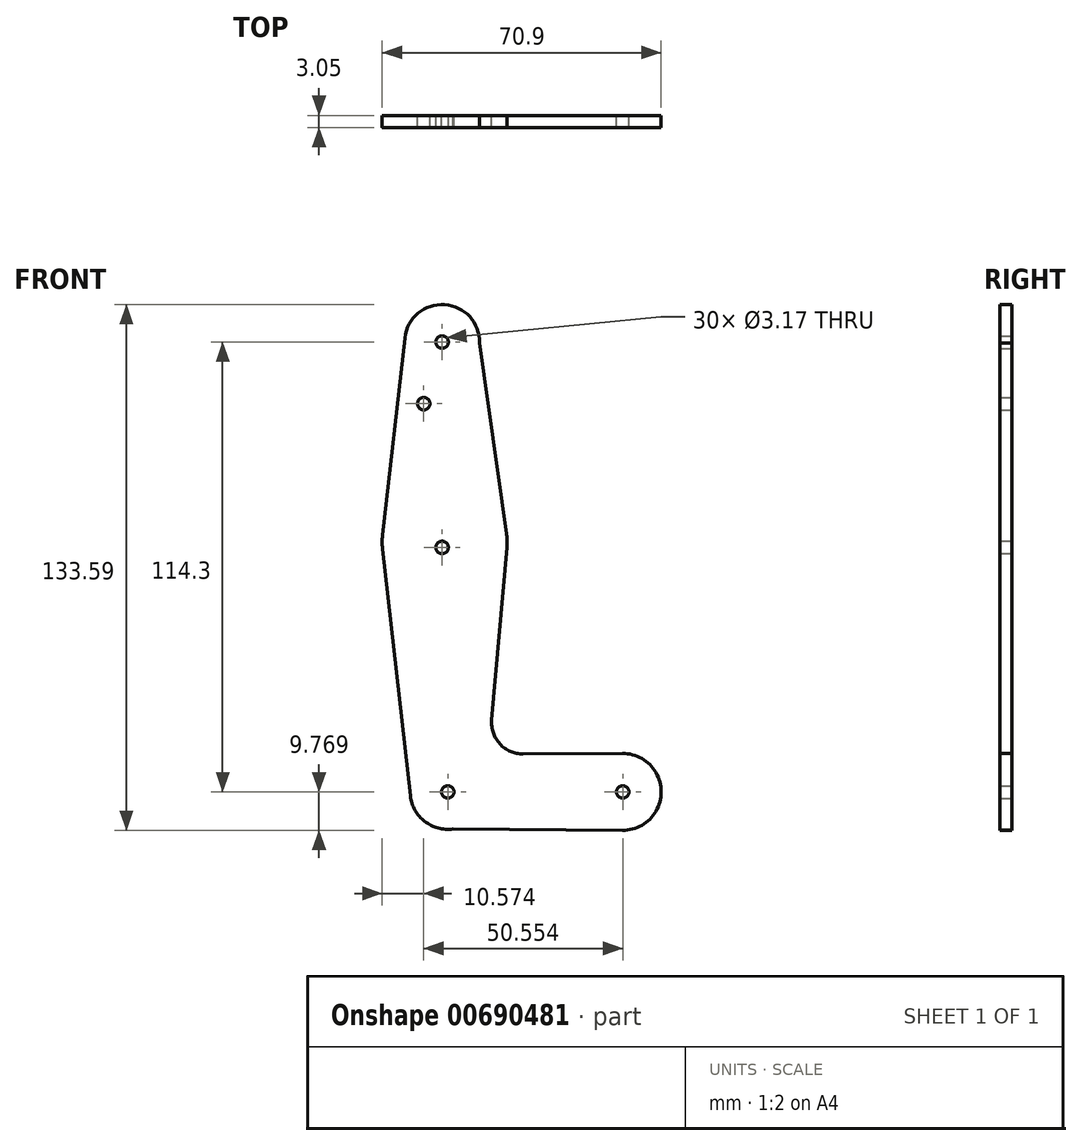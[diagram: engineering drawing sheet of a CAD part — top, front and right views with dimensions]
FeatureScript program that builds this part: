
annotation { "Feature Type Name" : "Feature", "Feature Type Description" : "" }
export const myFeature = defineFeature(function(context is Context, id is Id, definition is map)
    precondition{}
    {
        {
            var Q0;
            Q0=qCreatedBy(makeId("Front.planeOp"),FACE);
            var sketch = newSketch(context, id + "F0", { "sketchPlane" : qUnion([Q0])});
            skLineSegment(sketch, "E0", {"start": v(0, 52.19) * mm, "end": v(1.44, -62.11) * mm, "construction": true});
            skLineSegment(sketch, "E1", {"start": v(1.44, -62.11) * mm, "end": v(45.89, -62.11) * mm, "construction": true});
            skCircle(sketch, "E2", {"center": v(0, 52.19) * mm, "radius": 9.53 * mm});
            skCircle(sketch, "E3", {"center": v(1.44, -62.11) * mm, "radius": 9.53 * mm});
            skCircle(sketch, "E4", {"center": v(45.89, -62.11) * mm, "radius": 9.77 * mm});
            skCircle(sketch, "E5", {"center": v(0.64, 1.39) * mm, "radius": 15.88 * mm});
            skLineSegment(sketch, "E6", {"start": v(-9.46, 53.26) * mm, "end": v(-15.14, 3.17) * mm});
            skLineSegment(sketch, "E7", {"start": v(9.52, 51.98) * mm, "end": v(16.36, 3.6) * mm});
            skLineSegment(sketch, "E8", {"start": v(-15.14, -0.4) * mm, "end": v(-8.03, -63.18) * mm});
            skLineSegment(sketch, "E9", {"start": v(16.45, 0) * mm, "end": v(12.6, -43.84) * mm});
            skLineSegment(sketch, "E10", {"start": v(20.57, -52.48) * mm, "end": v(45.83, -52.34) * mm});
            skLineSegment(sketch, "E11", {"start": v(0, -71.53) * mm, "end": v(47.79, -71.9) * mm});
            skCircle(sketch, "E12", {"center": v(0, 52.19) * mm, "radius": 1.59 * mm});
            skCircle(sketch, "E13", {"center": v(0, 0) * mm, "radius": 1.59 * mm});
            skCircle(sketch, "E14", {"center": v(1.44, -62.11) * mm, "radius": 1.59 * mm});
            skCircle(sketch, "E15", {"center": v(45.89, -62.11) * mm, "radius": 1.59 * mm});
            skCircle(sketch, "E16", {"center": v(-4.67, 36.53) * mm, "radius": 1.59 * mm});
            skArc(sketch, "E17.filletArc", {"start": v(12.6, -43.84) * mm, "mid": v(14.68, -49.92) * mm, "end": v(20.57, -52.48) * mm});
            skSolve(sketch);
        }
        {
            var Q0;
            Q0 = qSketchRegion(id + "F0", true);
            extrude(context, id + "F1", {"entities" : qUnion([Q0]), "depth" : 3.05 * mm, "offsetDistance" : 25.4 * mm});
        }
    });
